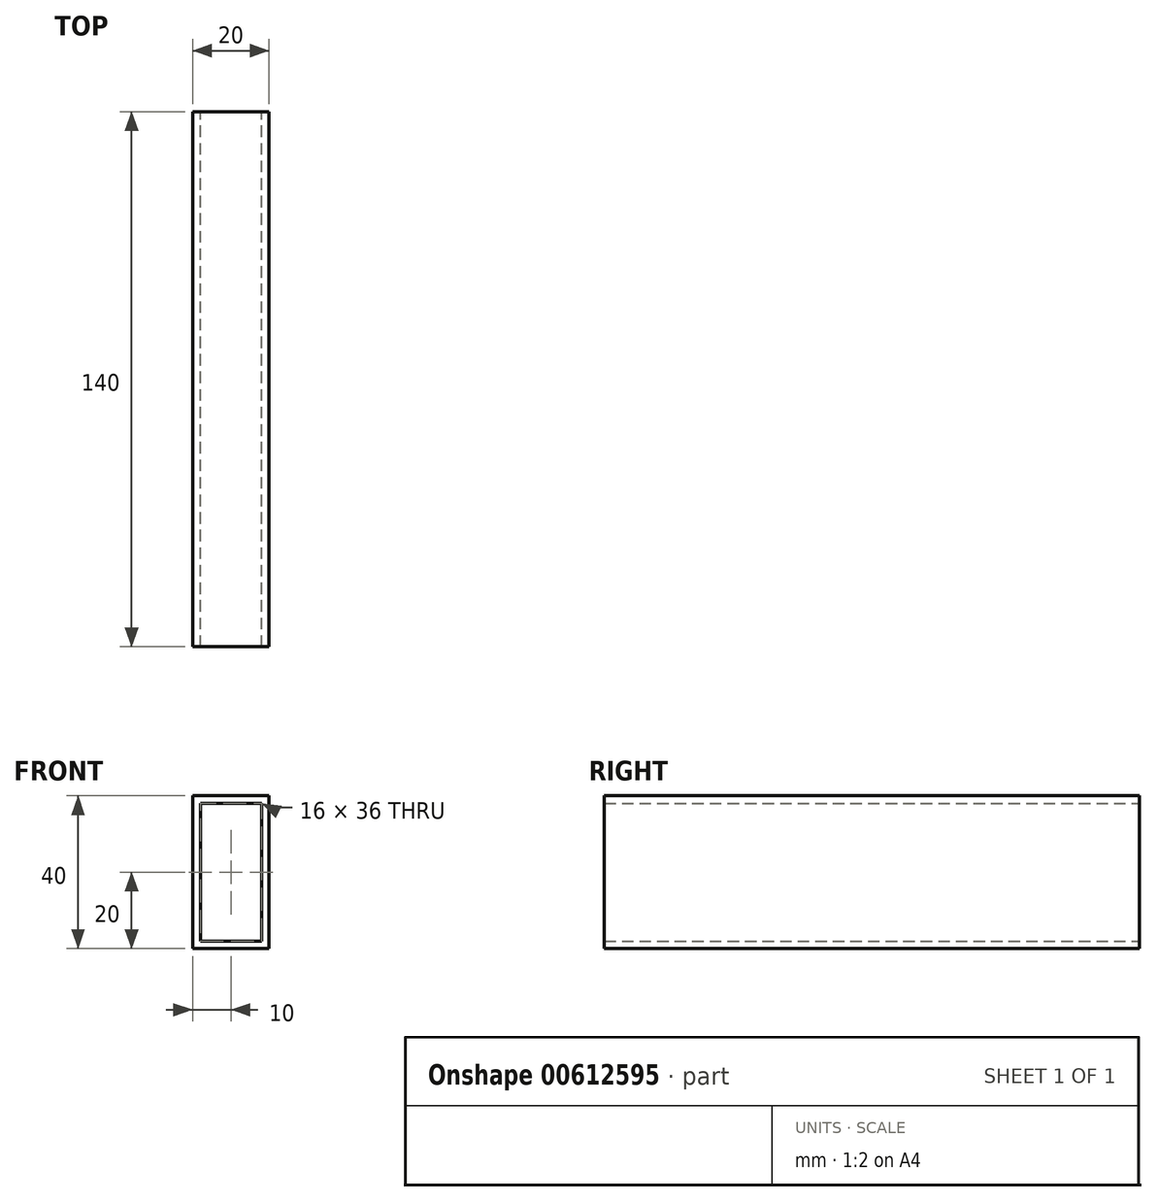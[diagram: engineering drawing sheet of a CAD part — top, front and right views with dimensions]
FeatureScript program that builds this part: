
annotation { "Feature Type Name" : "Feature", "Feature Type Description" : "" }
export const myFeature = defineFeature(function(context is Context, id is Id, definition is map)
    precondition{}
    {
        {
            var Q0;
            Q0=qCreatedBy(makeId("Front.planeOp"),FACE);
            var sketch = newSketch(context, id + "F0", { "sketchPlane" : qUnion([Q0])});
            skLineSegment(sketch, "E0.bottom", {"start": v(0, 0) * mm, "end": v(20, 0) * mm});
            skLineSegment(sketch, "E0.top", {"start": v(0, -40) * mm, "end": v(20, -40) * mm});
            skLineSegment(sketch, "E0.left", {"start": v(0, 0) * mm, "end": v(0, -40) * mm});
            skLineSegment(sketch, "E0.right", {"start": v(20, 0) * mm, "end": v(20, -40) * mm});
            skLineSegment(sketch, "E1.0", {"start": v(2, -2) * mm, "end": v(18, -2) * mm});
            skLineSegment(sketch, "E1.1", {"start": v(2, -2) * mm, "end": v(2, -38) * mm});
            skLineSegment(sketch, "E1.2", {"start": v(2, -38) * mm, "end": v(18, -38) * mm});
            skLineSegment(sketch, "E1.3", {"start": v(18, -2) * mm, "end": v(18, -38) * mm});
            skSolve(sketch);
        }
        {
            var Q0;
            Q0=makeQuery(id+"F0.imprint","IMPRINT",FACE,{"disambiguationData":[TD([[makeQuery(id+"F0.imprint","IMPRINT",EDGE,{"derivedFrom":sQuery(id+"F0.wireOp",EDGE,"E0.bottom")}),-1.0]])]});
            extrude(context, id + "F1", {"entities" : qUnion([Q0]), "depth" : 140 * mm, "offsetDistance" : 25.4 * mm});
        }
    });
